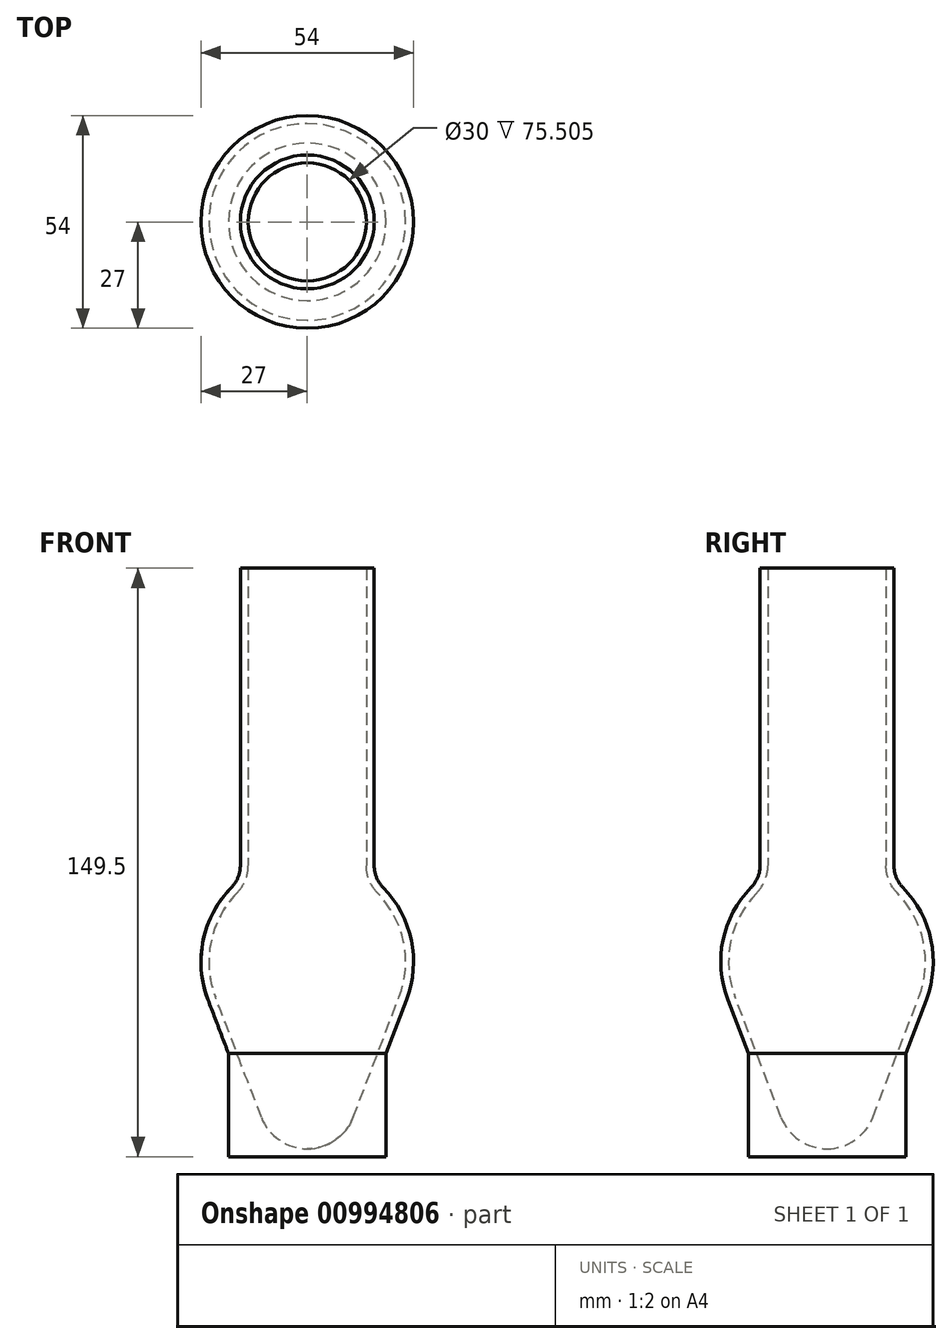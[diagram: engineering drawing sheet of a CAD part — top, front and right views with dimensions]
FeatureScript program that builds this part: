
annotation { "Feature Type Name" : "Feature", "Feature Type Description" : "" }
export const myFeature = defineFeature(function(context is Context, id is Id, definition is map)
    precondition{}
    {
        {
            var Q0;
            Q0=qCreatedBy(makeId("Front.planeOp"),FACE);
            var sketch = newSketch(context, id + "F0", { "sketchPlane" : qUnion([Q0])});
            skArc(sketch, "E0", {"start": v(23.35, -8.93) * mm, "mid": v(24.48, 5.09) * mm, "end": v(17.86, 17.5) * mm});
            skLineSegment(sketch, "E1", {"start": v(15, 100) * mm, "end": v(15, 24.5) * mm});
            skArc(sketch, "E2", {"start": v(0, -47.5) * mm, "mid": v(7.09, -45.3) * mm, "end": v(11.68, -39.46) * mm});
            skLineSegment(sketch, "E3", {"start": v(23.35, -8.93) * mm, "end": v(11.68, -39.46) * mm});
            skPoint(sketch, "E4.orphan", {"position": v(15, 0) * mm});
            skLineSegment(sketch, "E5", {"start": v(0, -47.5) * mm, "end": v(0, -49.5) * mm});
            skLineSegment(sketch, "E6", {"start": v(0, -49.5) * mm, "end": v(20, -49.5) * mm});
            skPoint(sketch, "E7.orphan", {"position": v(0, -51) * mm});
            skPoint(sketch, "E8.visualSharp", {"position": v(15, 20) * mm});
            skArc(sketch, "E8.filletArc", {"start": v(15, 24.5) * mm, "mid": v(15.74, 20.72) * mm, "end": v(17.86, 17.5) * mm});
            skLineSegment(sketch, "E9.0", {"start": v(17, 100) * mm, "end": v(17, 24.5) * mm});
            skArc(sketch, "E9.1", {"start": v(17, 24.5) * mm, "mid": v(17.6, 21.47) * mm, "end": v(19.29, 18.9) * mm});
            skArc(sketch, "E9.2", {"start": v(25.22, -9.64) * mm, "mid": v(26.43, 5.5) * mm, "end": v(19.29, 18.9) * mm});
            skLineSegment(sketch, "E9.3", {"start": v(25.22, -9.64) * mm, "end": v(20, -23.3) * mm});
            skLineSegment(sketch, "E10", {"start": v(15, 100) * mm, "end": v(17, 100) * mm});
            skLineSegment(sketch, "E11", {"start": v(20, -49.5) * mm, "end": v(20, -23.3) * mm});
            skLineSegment(sketch, "E12", {"start": v(0, 0) * mm, "end": v(0, 111.14) * mm});
            skSolve(sketch);
        }
        {
            var Q0;
            Q0=qSketchRegion(id+"F0",true);
            var Q1;
            Q1=sQuery(id+"F0.wireOp",EDGE,"E12");
            revolve(context, id + "F1", {"surfaceOperationType" : NewSurfaceOperationType.NEW, "entities" : qUnion([Q0]), "axis" : qUnion([Q1]), "revolveType" : RevolveType.FULL});
        }
    });
